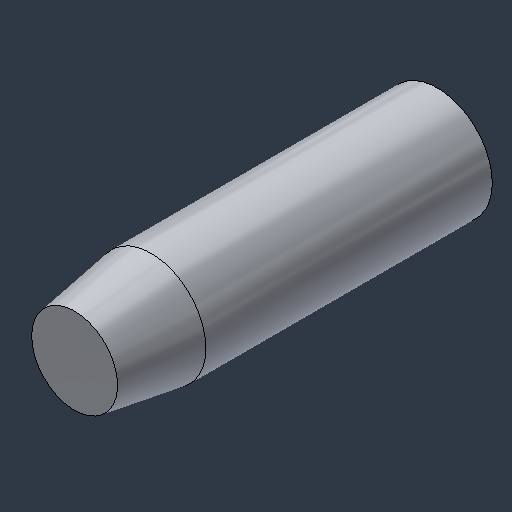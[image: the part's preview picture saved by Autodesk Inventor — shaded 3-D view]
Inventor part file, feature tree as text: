
AUTODESK INVENTOR PART (.ipt)
format: ipt  version: 2024.3 (Build 283343000, 343)  size: 110,080 bytes
history: native  units: mm (DEFAULTED — no unit token found)
features: chamfer x1
ambient origin geometry x8: Origin, YZ Plane, XZ Plane, XY Plane, X Axis, Y Axis, Z Axis, Center Point
bodies: Solid1 (feature_tree)
feature tree (1):
  chamfer  "Chamfer1"  [1 undecoded]
note: 1 required parameter value undecoded (feature->parameter linkage not recoverable at this tier; creation-order binding heuristic only, values carry confidence <= 0.55)
